# Revit family: CREB1x4
name_source: partatom
category: Lighting Fixtures
units: mm (PartAtom-declared; Revit-internal decimal feet)

## family parameters
Always vertical = Yes
Cut with Voids When Loaded = No
Host = Ceiling
Light Source = Yes
OmniClass Number = 23.80.70.11.14.17
OmniClass Title = Direct/Indirect
Part Type = Normal
Room Calculation Point = No
Round Connector Dimension = Use Diameter
Shared = No

## types (2) — shared parameters
Apparent Load = 31 VA
Assembly Code = D5020200
Color Filter = 16777215
Description = Cleanroom Recessed Ecology
Dimming Lamp Color Temperature Shift = <None>
Emit Shape Visible in Rendering = No
Emit from Rectangle Height = 0' - 0 1/32"
Emit from Rectangle Length = 3' - 11 3/4"
Emit from Rectangle Width = 0' - 11 3/4"
Housing Finish = Metal - Viscor - White
Lamp = LED
Lamp Wattage = 31 VA
Length = 3' - 11 3/4"
Lens Depth = 0' - 0 1/32"
Lens Finish = Acrylic - Viscor - Frosted White
Manufacturer = CERTOLUX by VISCOR
Model = CREB
Tilt Angle = 90.00°
URL = https://www.viscor.com
Voltage = 120 V
Width = 0' - 11 3/4"

## per-type parameters (varying)
| type | Photometric Web File | Water Shield |
| CREB1X4-LED840K035LUNV |  | <By Category> |
| CREB1X4-LED840K050LUNV | CREB1x4-LED840K035LUNV-P73P45.ies | Polycarbonate - Viscor - Clear Lens |

## geometry (parser evidence)
native form markers: Sweep x2
no freeform markers — native parametric forms only
